# Revit family: Slotted_Outlet-Unico-Plenum_Kit
name_source: partatom
category: Duct Accessories
units: mm (PartAtom-declared; Revit-internal decimal feet)

## family parameters
Always vertical = No
Cut with Voids When Loaded = No
OmniClass Number = 23.75.70.00
OmniClass Title = HVAC Distribution Devices
Part Type = Attaches To
Round Connector Dimension = Use Diameter
Shared = No
Work Plane-Based = Yes

## types (1)
- UPC-101
    Assembly Code = D3040100
    Default Elevation = 48"
    Description = Slotted Outlet Plenum Kit
    Duct Connection Diameter = 3"
    Finish = Paint - Unico - White
    Height = 1 3/4"
    Instruction Sheet Link = https://www.unicosystem.com
    Keynote = 23 30 00
    Manufacturer = Unico, Inc.
    Manufacturer Fax Number = 314-457-9000
    Model = UPC-101
    Performance URL = https://www.unicosystem.com
    URL = https://www.unicosystem.com
    Version = 2020 - v1.0a
    Video Link = https://www.youtube.com
    Warranty URL = https://www.unicosystem.com
    Width = 10 3/8"

## geometry (parser evidence)
native form markers: Sweep x5
no freeform markers — native parametric forms only
